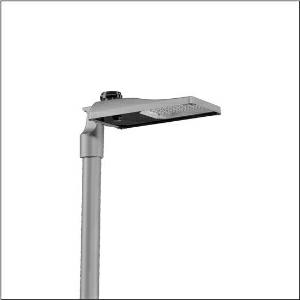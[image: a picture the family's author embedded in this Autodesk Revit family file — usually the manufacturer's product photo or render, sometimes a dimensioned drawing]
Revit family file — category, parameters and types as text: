
# Revit family: streetlight_sl_31_mini___st1_0a_5xh2d35m08ga_46b7
name_source: partatom
category: Lighting Fixtures
units: mm (PartAtom-declared; Revit-internal decimal feet)

## family parameters
Cut with Voids When Loaded = No
Host = Face
Light Source = No
Part Type = Normal
Room Calculation Point = No
Round Connector Dimension = Use Diameter
Shared = No

## types (1)
- --- (1 x LED, 5880 lm, 39.3 W, 3000K)
    Apparent Load = 39 VA
    CIE Flux Codes = 37 72 97 100 100
    Color Rendering = 70
    Color Temperature = 3000K
    Default Elevation = 1800 mm
    Description = Streetlight SL 31 mini NEMA (7pin), Desk-Remote mast luminaire for post-top, side-entry; light control with lens of PMMA; light distribution: ST1.0a, direct asymmetric distribution, for standard-compliant lighting for roads and squares; LED: luminous flux: 5.880lm, light colour: 730, colour temperature: 3000K; luminous efficacy: 149,6lm/W; control: pre-setting: linear dimming characteristic, flexible luminous flux parameterisation, time-dependent luminous flux control, constant luminous flux control, intelligent temperature release in ECG and LED module, overheat protection; luminaire housing, of diecast aluminium, SITECO metallic grey (DB 702S), corrosivity category C5 high according to DIN EN ISO 12944; cover of toughened safety glass, transparent, mast flange of diecast aluminium, SITECO metallic grey (DB 702S), spigot size: 76/60mm, mast flange included unmounted; cable length: 6,5m, connection cable pre-assembled; mains connection: 220..240V, AC, 50/60Hz; power consumption (at start of service life): 39,3W / (at end of service life): 40,7W / (with reduced operation 50%): 18,1W; protection rating (complete): IP66; insulation class (complete): insulation class I (protective earthing); impact resistance: IK09; certification: CE, ENEC, ENEC+, VDE, UKCA; permissible operating ambient temperature for outdoor applications: -40..+50°C; packaging unit: 1 piece

Light Distribution: ST1.0a
    Height = 76 mm
    Lamp = 1 x LED
    Lamp Light Flux = 5880 lm
    Lamp Power = 39.3 W
    Lamp count = 1
    Length = 547 mm
    Luminous efficacy = 150 lm/W
    Manufacturer = Siteco
    ModVariant = No
    Model = 5XH2D35M08GA
    Number of Poles = 1
    OnlyDefault = Yes
    Power Factor = 1
    Product Name = Streetlight SL 31 mini | ST1.0a
    Product group = mast luminaire | pylon top
    ProductGroupID = 6100
    Protection Class = Protection class I
    Protection Degree = IP 66
    RLX_Detail_Level = 1
    RLX_Emergency_Light_Flux = 0 lm
    RLX_Emergency_Type = 0
    RLX_Emergency_Type_DB = No
    RlxData = <blob elided: 40213 chars, md5=f3bb51e8>
    Socket = socket
    Standby Power = 0 W
    System Light Flux = 5880 lm
    System Power = 39 W
    Type Comments = factory setting: luminous flux: 100 % | dim-lin: 254 | 798 mA
    Type Image = l_1300324.jpg
    URL = http://relux.com
    VarID = @adj_061177
    Voltage = 0 V
    Weight = 0.00 kg
    Width = 265 mm

## geometry (parser evidence)
native form markers: Blend x4, Sweep x12
no freeform markers — native parametric forms only
